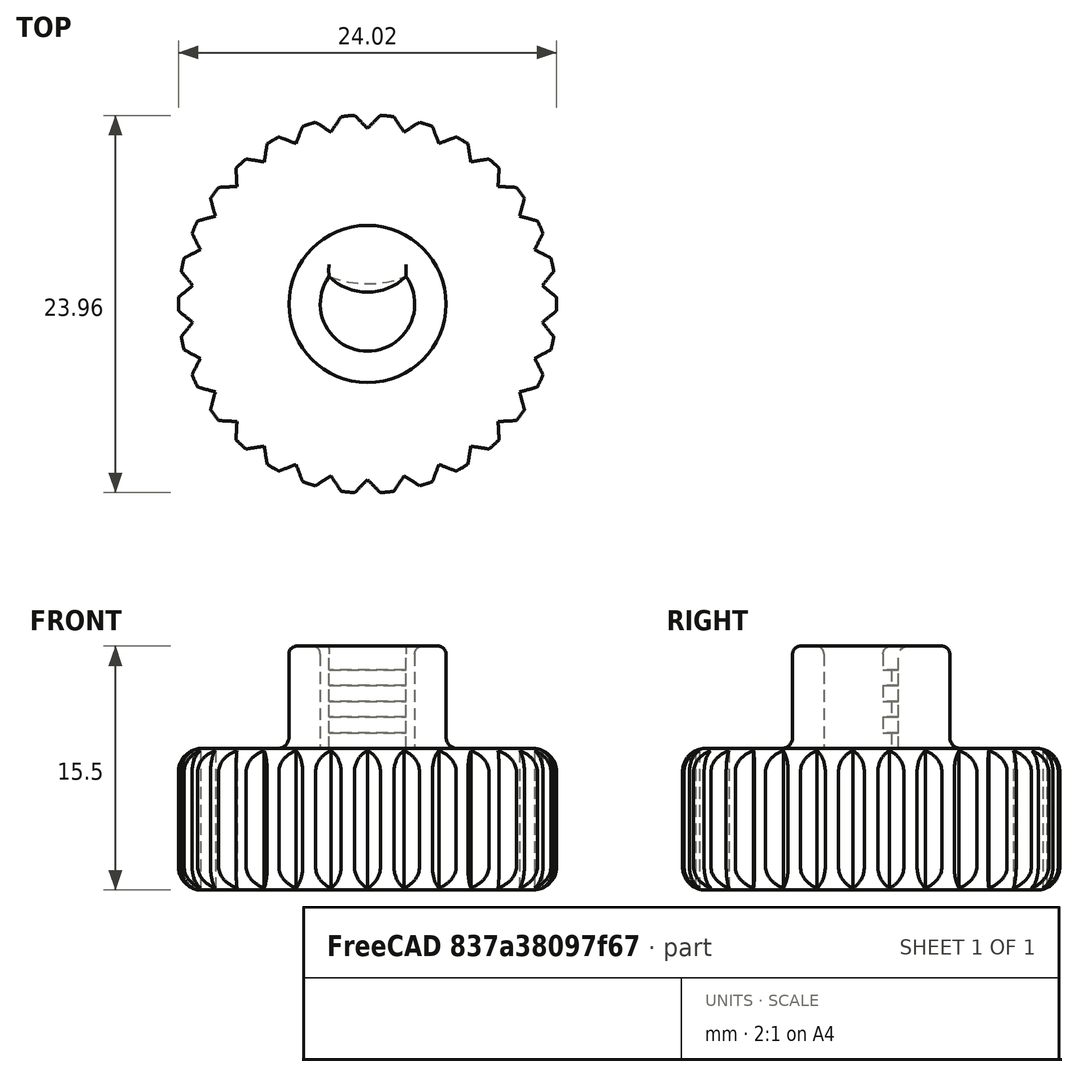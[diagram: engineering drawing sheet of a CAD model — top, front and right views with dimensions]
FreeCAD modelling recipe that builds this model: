
FCSTD DOCUMENT  (FreeCAD 0.17R13662 (Git))
Label: Universal_LCD_knob
License: All rights reserved
LicenseURL: http://en.wikipedia.org/wiki/All_rights_reserved
objects: Sketcher::SketchObject×6, PartDesign::Fillet×4, PartDesign::Pocket×4, PartDesign::Pad×2, Mesh::Feature×1, PartDesign::PolarPattern×1, PartDesign::Body×1, Part::Feature×1
note: 25 computed .brp shape members not serialized (recipe doc carries the construction recipe); baked Part::Feature solids carry a one-line shape summary decoded from their .brp

FEATURE [Mesh::Feature] Universal_LCD_Knob  label="Universal LCD Knob"
  Placement = pos=(-5,-2,0) rot=(0,0,1;0rad)
FEATURE [Sketcher::SketchObject] Sketch
  MapMode = 5
  Support = -> [XY_Plane]
  sketch-geometry (1):
    g0: Circle CenterX=0 CenterY=0 CenterZ=0 NormalX=0 NormalY=0 NormalZ=1 AngleXU=0 Radius=12.0115
  constraints (1):
    c: Coincident(g0,g-1)
FEATURE [PartDesign::Pad] Pad
  Length = 9
  Length2 = 100
  Profile = -> Sketch
  Type = 0
FEATURE [Sketcher::SketchObject] Sketch001
  MapMode = 5
  Placement = pos=(0,0,9) rot=(0,0,1;0rad)
  Support = -> [Pad]
  sketch-geometry (3):
    g0: Circle CenterX=0 CenterY=0 CenterZ=0 NormalX=0 NormalY=0 NormalZ=1 AngleXU=0 Radius=4.9907
    g1: ArcOfCircle CenterX=0 CenterY=0 CenterZ=0 NormalX=0 NormalY=0 NormalZ=1 AngleXU=0 Radius=3 StartAngle=2.52256 EndAngle=6.90342
    g2: ArcOfCircle CenterX=-0.00257252 CenterY=4.27017 CenterZ=0 NormalX=0 NormalY=0 NormalZ=1 AngleXU=0 Radius=3.515 StartAngle=3.94483 EndAngle=5.48115
  constraints (6):
    c: Coincident(g0,g-1)
    c: Coincident(g1,g-1)
    c: Radius(g1) = 3
    c: Radius(g2) = 3.515
    c: Coincident(g1,g2)
    c: Coincident(g1,g2)
FEATURE [PartDesign::Pad] Pad001
  BaseFeature = -> Pad
  Length = 6.5
  Length2 = 100
  Profile = -> Sketch001
  Type = 0
FEATURE [Sketcher::SketchObject] Sketch002
  MapMode = 5
  Placement = pos=(0,0,9) rot=(0,0,1;0rad)
  Support = -> [Pad001]
  sketch-geometry (4):
    g0: LineSegment StartX=-1.31766 StartY=12.4733 StartZ=0 EndX=0 EndY=11.1596 EndZ=0
    g1: LineSegment StartX=-1.31766 StartY=12.4733 StartZ=0 EndX=0 EndY=12.3383 EndZ=0
    g2: LineSegment StartX=1.31766 StartY=12.4733 StartZ=0 EndX=0 EndY=12.3383 EndZ=0
    g3: LineSegment StartX=1.31766 StartY=12.4733 StartZ=0 EndX=0 EndY=11.1596 EndZ=0
  constraints (4):
    c: PointOnObject(g0,g-2)
    c: Coincident(g1,g0)
    c: PointOnObject(g1,g-2)
    c: Coincident(g2,g3)
FEATURE [PartDesign::Fillet] Fillet
  Base = -> Pad001 [Edge3,Edge2]
  BaseFeature = -> Pad001
  Radius = 1.5
FEATURE [PartDesign::Pocket] Pocket
  BaseFeature = -> Fillet
  Length = 5
  Length2 = 100
  Profile = -> Sketch002
  Type = 1
FEATURE [PartDesign::PolarPattern] PolarPattern
  Angle = 360
  Axis = -> Sketch002 [N_Axis]
  BaseFeature = -> Pocket
  Occurrences = 30
  Originals = -> [Pocket]
FEATURE [PartDesign::Fillet] Fillet001
  Base = -> PolarPattern [Edge278]
  BaseFeature = -> PolarPattern
  Radius = 0.7
FEATURE [Sketcher::SketchObject] Sketch003
  ExternalGeometry = -> [Fillet001]
  MapMode = 5
  Placement = pos=(0,0,9) rot=(0,0,1;0rad)
  Support = -> [Fillet001]
  sketch-geometry (2):
    g0: ArcOfCircle CenterX=-0.00487212 CenterY=8.08733 CenterZ=0 NormalX=0 NormalY=0 NormalZ=1 AngleXU=0 Radius=6.7989 StartAngle=4.34556 EndAngle=5.08042
    g1: ArcOfCircle CenterX=-0.00228361 CenterY=3.79062 CenterZ=0 NormalX=0 NormalY=0 NormalZ=1 AngleXU=0 Radius=3.18757 StartAngle=3.84011 EndAngle=5.58587
  constraints (4):
    c: Coincident(g0,g-3)
    c: Coincident(g0,g-3)
    c: Coincident(g1,g0)
    c: Coincident(g1,g0)
FEATURE [PartDesign::Pocket] Pocket001
  BaseFeature = -> Fillet001
  Length = 1
  Length2 = 100
  Profile = -> Sketch003
  Reversed = true
  Type = 0
FEATURE [Sketcher::SketchObject] Sketch004
  ExternalGeometry = -> [Fillet001]
  Placement = pos=(0,0,11) rot=(0,0,1;0rad)
  sketch-geometry (2):
    g0: ArcOfCircle CenterX=-0.00487212 CenterY=8.08733 CenterZ=0 NormalX=0 NormalY=0 NormalZ=1 AngleXU=0 Radius=6.7989 StartAngle=4.34556 EndAngle=5.08042
    g1: ArcOfCircle CenterX=-0.00228361 CenterY=3.79062 CenterZ=0 NormalX=0 NormalY=0 NormalZ=1 AngleXU=0 Radius=3.18757 StartAngle=3.84011 EndAngle=5.58587
  constraints (4):
    c: Coincident(g0,g-3)
    c: Coincident(g0,g-3)
    c: Coincident(g1,g0)
    c: Coincident(g1,g0)
FEATURE [PartDesign::Pocket] Pocket002
  BaseFeature = -> Pocket001
  Length = 1
  Length2 = 100
  Profile = -> Sketch004
  Reversed = true
  Type = 0
FEATURE [Sketcher::SketchObject] Sketch005
  ExternalGeometry = -> [Fillet001]
  Placement = pos=(0,0,13) rot=(0,0,1;0rad)
  sketch-geometry (2):
    g0: ArcOfCircle CenterX=-0.00487212 CenterY=8.08733 CenterZ=0 NormalX=0 NormalY=0 NormalZ=1 AngleXU=0 Radius=6.7989 StartAngle=4.34556 EndAngle=5.08042
    g1: ArcOfCircle CenterX=-0.00228361 CenterY=3.79062 CenterZ=0 NormalX=0 NormalY=0 NormalZ=1 AngleXU=0 Radius=3.18757 StartAngle=3.84011 EndAngle=5.58587
  constraints (4):
    c: Coincident(g0,g-3)
    c: Coincident(g0,g-3)
    c: Coincident(g1,g0)
    c: Coincident(g1,g0)
FEATURE [PartDesign::Pocket] Pocket003
  BaseFeature = -> Pocket002
  Length = 1
  Length2 = 100
  Profile = -> Sketch005
  Reversed = true
  Type = 0
FEATURE [PartDesign::Fillet] Fillet002
  Base = -> Pocket003 [Edge281,Edge282]
  BaseFeature = -> Pocket003
  Radius = 0.5
FEATURE [PartDesign::Fillet] Fillet003
  Base = -> Fillet002 [Edge3]
  BaseFeature = -> Fillet002
  Radius = 0.5
FEATURE [PartDesign::Body] Body
  Group = -> [Sketch,Pad,Sketch001,Pad001,Fillet,Sketch002,Pocket,PolarPattern,Fillet001,Sketch003,Pocket001,Sketch004,Pocket002,Sketch005,Pocket003,Fillet002,Fillet003]
  Origin = -> Origin
FEATURE [Part::Feature] Fillet003001  label="Fillet004"
  shape: bbox 26 x 26 x 15.5 mm, 113 faces (baked)
